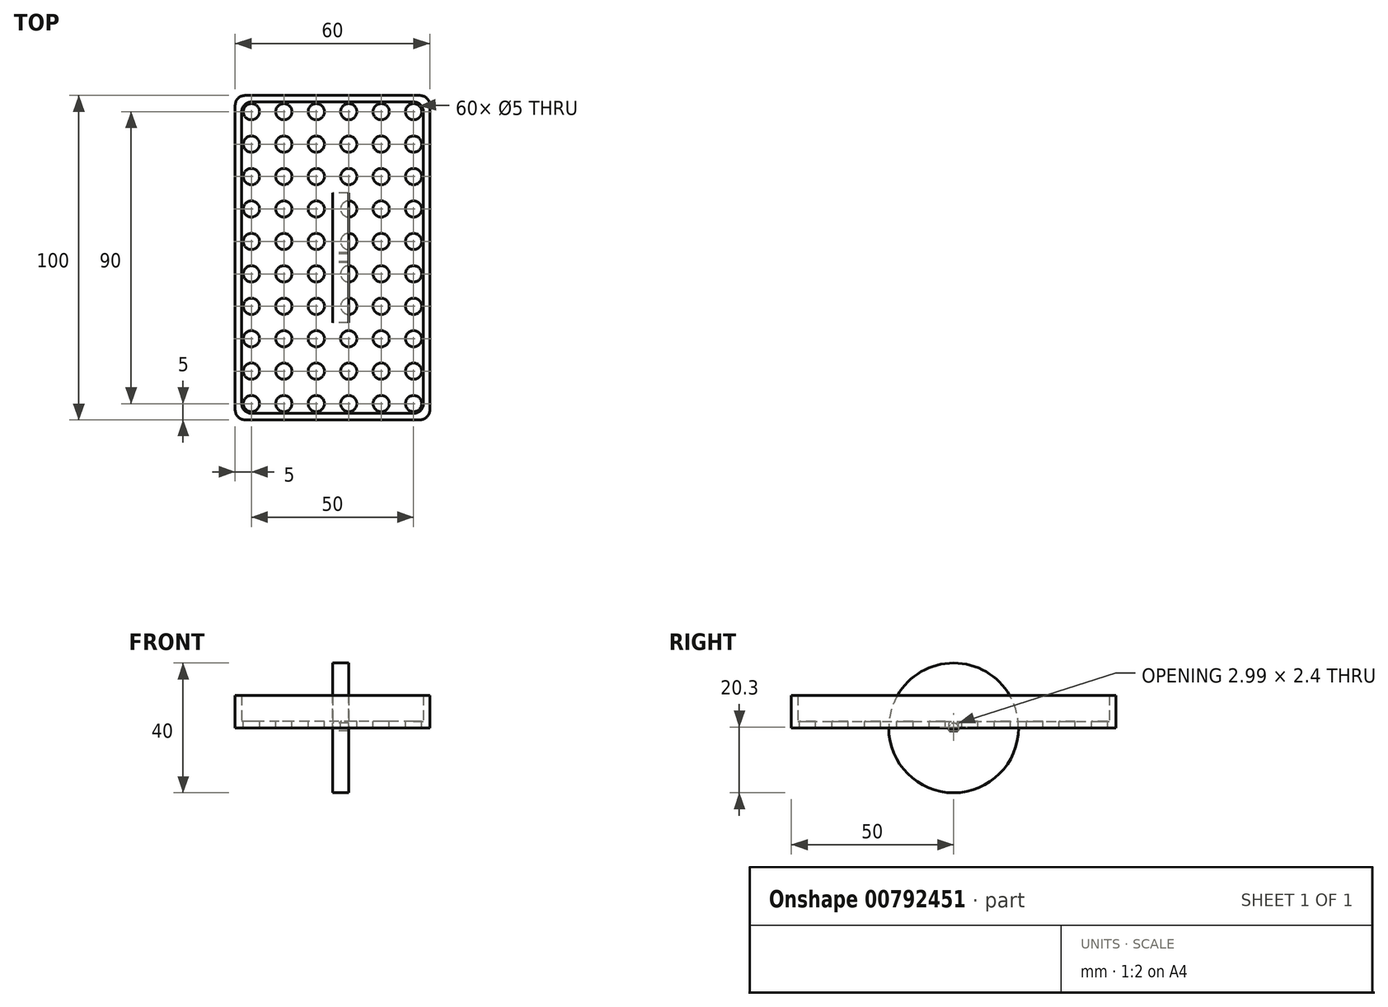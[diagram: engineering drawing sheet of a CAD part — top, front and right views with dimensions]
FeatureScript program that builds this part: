
annotation { "Feature Type Name" : "Feature", "Feature Type Description" : "" }
export const myFeature = defineFeature(function(context is Context, id is Id, definition is map)
    precondition{}
    {
        {
            var Q0;
            Q0=qCreatedBy(makeId("Top.planeOp"),FACE);
            var sketch = newSketch(context, id + "F0", { "sketchPlane" : qUnion([Q0])});
            skLineSegment(sketch, "E0.bottom", {"start": v(30, -50) * mm, "end": v(-30, -50) * mm});
            skLineSegment(sketch, "E0.top", {"start": v(30, 50) * mm, "end": v(-30, 50) * mm});
            skLineSegment(sketch, "E0.left", {"start": v(30, -50) * mm, "end": v(30, 50) * mm});
            skLineSegment(sketch, "E0.right", {"start": v(-30, -50) * mm, "end": v(-30, 50) * mm});
            skPoint(sketch, "E0.middle", {"position": v(0, 0) * mm});
            skSolve(sketch);
        }
        {
            var Q0;
            Q0=makeQuery(id+"F0.imprint","IMPRINT",FACE,{"disambiguationData":[TD([[makeQuery(id+"F0.imprint","IMPRINT",EDGE,{"derivedFrom":sQuery(id+"F0.wireOp",EDGE,"E0.bottom")}),-1.0]])]});
            extrude(context, id + "F1", {"entities" : qUnion([Q0]), "depth" : 10 * mm, "offsetDistance" : 25 * mm});
        }
        {
            var Q0;
            Q0=makeQuery(id+"F1.opExtrude","CAP_FACE",FACE,{"disambiguationData":[OSD([sQuery(id+"F0.wireOp",EDGE,"E0.bottom"),sQuery(id+"F0.wireOp",EDGE,"E0.top"),sQuery(id+"F0.wireOp",EDGE,"E0.left"),sQuery(id+"F0.wireOp",EDGE,"E0.right")])],"isStart":false});
            shell(context, id + "F2", {"entities" : qUnion([Q0]), "thickness" : 2 * mm});
        }
        {
            var Q0;
            Q0=makeQuery(id+"F2.opShell","OFFSET_FACE",FACE,{"disambiguationData":[OSD([sQuery(id+"F0.wireOp",EDGE,"E0.bottom"),sQuery(id+"F0.wireOp",EDGE,"E0.top"),sQuery(id+"F0.wireOp",EDGE,"E0.left"),sQuery(id+"F0.wireOp",EDGE,"E0.right")])]});
            var sketch = newSketch(context, id + "F3", { "sketchPlane" : qUnion([Q0])});
            skPoint(sketch, "E1", {"position": v(-25, 45) * mm});
            skPoint(sketch, "E2.0.1.0", {"position": v(-25, 35) * mm});
            skPoint(sketch, "E2.0.2.0", {"position": v(-25, 25) * mm});
            skPoint(sketch, "E2.0.3.0", {"position": v(-25, 15) * mm});
            skPoint(sketch, "E2.0.4.0", {"position": v(-25, 5) * mm});
            skPoint(sketch, "E2.0.5.0", {"position": v(-25, -5) * mm});
            skPoint(sketch, "E2.0.6.0", {"position": v(-25, -15) * mm});
            skPoint(sketch, "E2.0.7.0", {"position": v(-25, -25) * mm});
            skPoint(sketch, "E2.0.8.0", {"position": v(-25, -35) * mm});
            skPoint(sketch, "E2.0.9.0", {"position": v(-25, -45) * mm});
            skPoint(sketch, "E2.1.0.0", {"position": v(-15, 45) * mm});
            skPoint(sketch, "E2.1.1.0", {"position": v(-15, 35) * mm});
            skPoint(sketch, "E2.1.2.0", {"position": v(-15, 25) * mm});
            skPoint(sketch, "E2.1.3.0", {"position": v(-15, 15) * mm});
            skPoint(sketch, "E2.1.4.0", {"position": v(-15, 5) * mm});
            skPoint(sketch, "E2.1.5.0", {"position": v(-15, -5) * mm});
            skPoint(sketch, "E2.1.6.0", {"position": v(-15, -15) * mm});
            skPoint(sketch, "E2.1.7.0", {"position": v(-15, -25) * mm});
            skPoint(sketch, "E2.1.8.0", {"position": v(-15, -35) * mm});
            skPoint(sketch, "E2.1.9.0", {"position": v(-15, -45) * mm});
            skPoint(sketch, "E2.2.0.0", {"position": v(-5, 45) * mm});
            skPoint(sketch, "E2.2.1.0", {"position": v(-5, 35) * mm});
            skPoint(sketch, "E2.2.2.0", {"position": v(-5, 25) * mm});
            skPoint(sketch, "E2.2.3.0", {"position": v(-5, 15) * mm});
            skPoint(sketch, "E2.2.4.0", {"position": v(-5, 5) * mm});
            skPoint(sketch, "E2.2.5.0", {"position": v(-5, -5) * mm});
            skPoint(sketch, "E2.2.6.0", {"position": v(-5, -15) * mm});
            skPoint(sketch, "E2.2.7.0", {"position": v(-5, -25) * mm});
            skPoint(sketch, "E2.2.8.0", {"position": v(-5, -35) * mm});
            skPoint(sketch, "E2.2.9.0", {"position": v(-5, -45) * mm});
            skPoint(sketch, "E2.3.0.0", {"position": v(5, 45) * mm});
            skPoint(sketch, "E2.3.1.0", {"position": v(5, 35) * mm});
            skPoint(sketch, "E2.3.2.0", {"position": v(5, 25) * mm});
            skPoint(sketch, "E2.3.3.0", {"position": v(5, 15) * mm});
            skPoint(sketch, "E2.3.4.0", {"position": v(5, 5) * mm});
            skPoint(sketch, "E2.3.5.0", {"position": v(5, -5) * mm});
            skPoint(sketch, "E2.3.6.0", {"position": v(5, -15) * mm});
            skPoint(sketch, "E2.3.7.0", {"position": v(5, -25) * mm});
            skPoint(sketch, "E2.3.8.0", {"position": v(5, -35) * mm});
            skPoint(sketch, "E2.3.9.0", {"position": v(5, -45) * mm});
            skPoint(sketch, "E2.4.0.0", {"position": v(15, 45) * mm});
            skPoint(sketch, "E2.4.1.0", {"position": v(15, 35) * mm});
            skPoint(sketch, "E2.4.2.0", {"position": v(15, 25) * mm});
            skPoint(sketch, "E2.4.3.0", {"position": v(15, 15) * mm});
            skPoint(sketch, "E2.4.4.0", {"position": v(15, 5) * mm});
            skPoint(sketch, "E2.4.5.0", {"position": v(15, -5) * mm});
            skPoint(sketch, "E2.4.6.0", {"position": v(15, -15) * mm});
            skPoint(sketch, "E2.4.7.0", {"position": v(15, -25) * mm});
            skPoint(sketch, "E2.4.8.0", {"position": v(15, -35) * mm});
            skPoint(sketch, "E2.4.9.0", {"position": v(15, -45) * mm});
            skPoint(sketch, "E2.5.0.0", {"position": v(25, 45) * mm});
            skPoint(sketch, "E2.5.1.0", {"position": v(25, 35) * mm});
            skPoint(sketch, "E2.5.2.0", {"position": v(25, 25) * mm});
            skPoint(sketch, "E2.5.3.0", {"position": v(25, 15) * mm});
            skPoint(sketch, "E2.5.4.0", {"position": v(25, 5) * mm});
            skPoint(sketch, "E2.5.5.0", {"position": v(25, -5) * mm});
            skPoint(sketch, "E2.5.6.0", {"position": v(25, -15) * mm});
            skPoint(sketch, "E2.5.7.0", {"position": v(25, -25) * mm});
            skPoint(sketch, "E2.5.8.0", {"position": v(25, -35) * mm});
            skPoint(sketch, "E2.5.9.0", {"position": v(25, -45) * mm});
            skLineSegment(sketch, "E2.direction1", {"start": v(-25, 45) * mm, "end": v(-15, 45) * mm, "construction": true});
            skLineSegment(sketch, "E2.direction2", {"start": v(-25, 45) * mm, "end": v(-25, 35) * mm, "construction": true});
            skLineSegment(sketch, "E3", {"start": v(5, 5) * mm, "end": v(-5, -5) * mm, "construction": true});
            skPoint(sketch, "E4", {"position": v(0, 0) * mm});
            skSolve(sketch);
        }
        {
            var Q0;
            Q0=sQuery(id+"F3.wireOp",VERTEX,"E2.1.1.0");
            var Q1;
            Q1=sQuery(id+"F3.wireOp",VERTEX,"E2.4.1.0");
            var Q2;
            Q2=sQuery(id+"F3.wireOp",VERTEX,"E1");
            var Q3;
            Q3=sQuery(id+"F3.wireOp",VERTEX,"E2.1.0.0");
            var Q4;
            Q4=sQuery(id+"F3.wireOp",VERTEX,"E2.2.0.0");
            var Q5;
            Q5=sQuery(id+"F3.wireOp",VERTEX,"E2.3.0.0");
            var Q6;
            Q6=sQuery(id+"F3.wireOp",VERTEX,"E2.4.0.0");
            var Q7;
            Q7=sQuery(id+"F3.wireOp",VERTEX,"E2.5.0.0");
            var Q8;
            Q8=sQuery(id+"F3.wireOp",VERTEX,"E2.3.3.0");
            var Q9;
            Q9=sQuery(id+"F3.wireOp",VERTEX,"E2.1.2.0");
            var Q10;
            Q10=sQuery(id+"F3.wireOp",VERTEX,"E2.5.5.0");
            var Q11;
            Q11=sQuery(id+"F3.wireOp",VERTEX,"E2.1.3.0");
            var Q12;
            Q12=sQuery(id+"F3.wireOp",VERTEX,"E2.3.6.0");
            var Q13;
            Q13=sQuery(id+"F3.wireOp",VERTEX,"E2.1.4.0");
            var Q14;
            Q14=sQuery(id+"F3.wireOp",VERTEX,"E2.5.2.0");
            var Q15;
            Q15=sQuery(id+"F3.wireOp",VERTEX,"E2.4.6.0");
            var Q16;
            Q16=sQuery(id+"F3.wireOp",VERTEX,"E2.0.6.0");
            var Q17;
            Q17=sQuery(id+"F3.wireOp",VERTEX,"E2.4.7.0");
            var Q18;
            Q18=sQuery(id+"F3.wireOp",VERTEX,"E2.0.3.0");
            var Q19;
            Q19=sQuery(id+"F3.wireOp",VERTEX,"E2.3.9.0");
            var Q20;
            Q20=sQuery(id+"F3.wireOp",VERTEX,"E2.4.2.0");
            var Q21;
            Q21=sQuery(id+"F3.wireOp",VERTEX,"E2.0.9.0");
            var Q22;
            Q22=sQuery(id+"F3.wireOp",VERTEX,"E2.1.9.0");
            var Q23;
            Q23=sQuery(id+"F3.wireOp",VERTEX,"E2.4.3.0");
            var Q24;
            Q24=sQuery(id+"F3.wireOp",VERTEX,"E2.2.8.0");
            var Q25;
            Q25=sQuery(id+"F3.wireOp",VERTEX,"E2.5.9.0");
            var Q26;
            Q26=sQuery(id+"F3.wireOp",VERTEX,"E2.direction2.end");
            var Q27;
            Q27=sQuery(id+"F3.wireOp",VERTEX,"E2.2.4.0");
            var Q28;
            Q28=sQuery(id+"F3.wireOp",VERTEX,"E2.2.5.0");
            var Q29;
            Q29=sQuery(id+"F3.wireOp",VERTEX,"E2.4.9.0");
            var Q30;
            Q30=sQuery(id+"F3.wireOp",VERTEX,"E2.5.1.0");
            var Q31;
            Q31=sQuery(id+"F3.wireOp",VERTEX,"E2.3.5.0");
            var Q32;
            Q32=sQuery(id+"F3.wireOp",VERTEX,"E2.0.5.0");
            var Q33;
            Q33=sQuery(id+"F3.wireOp",VERTEX,"E2.4.5.0");
            var Q34;
            Q34=sQuery(id+"F3.wireOp",VERTEX,"E2.0.7.0");
            var Q35;
            Q35=sQuery(id+"F3.wireOp",VERTEX,"E2.1.8.0");
            var Q36;
            Q36=sQuery(id+"F3.wireOp",VERTEX,"E2.2.3.0");
            var Q37;
            Q37=sQuery(id+"F3.wireOp",VERTEX,"E2.5.7.0");
            var Q38;
            Q38=sQuery(id+"F3.wireOp",VERTEX,"E2.2.6.0");
            var Q39;
            Q39=sQuery(id+"F3.wireOp",VERTEX,"E2.3.4.0");
            var Q40;
            Q40=sQuery(id+"F3.wireOp",VERTEX,"E2.3.7.0");
            var Q41;
            Q41=sQuery(id+"F3.wireOp",VERTEX,"E2.5.3.0");
            var Q42;
            Q42=sQuery(id+"F3.wireOp",VERTEX,"E2.3.8.0");
            var Q43;
            Q43=sQuery(id+"F3.wireOp",VERTEX,"E2.5.4.0");
            var Q44;
            Q44=sQuery(id+"F3.wireOp",VERTEX,"E2.2.7.0");
            var Q45;
            Q45=sQuery(id+"F3.wireOp",VERTEX,"E2.0.8.0");
            var Q46;
            Q46=sQuery(id+"F3.wireOp",VERTEX,"E2.1.5.0");
            var Q47;
            Q47=sQuery(id+"F3.wireOp",VERTEX,"E2.1.7.0");
            var Q48;
            Q48=sQuery(id+"F3.wireOp",VERTEX,"E2.3.1.0");
            var Q49;
            Q49=sQuery(id+"F3.wireOp",VERTEX,"E2.2.1.0");
            var Q50;
            Q50=sQuery(id+"F3.wireOp",VERTEX,"E2.0.2.0");
            var Q51;
            Q51=sQuery(id+"F3.wireOp",VERTEX,"E2.2.2.0");
            var Q52;
            Q52=sQuery(id+"F3.wireOp",VERTEX,"E2.5.8.0");
            var Q53;
            Q53=sQuery(id+"F3.wireOp",VERTEX,"E2.1.6.0");
            var Q54;
            Q54=sQuery(id+"F3.wireOp",VERTEX,"E2.3.2.0");
            var Q55;
            Q55=sQuery(id+"F3.wireOp",VERTEX,"E2.4.8.0");
            var Q56;
            Q56=sQuery(id+"F3.wireOp",VERTEX,"E2.5.6.0");
            var Q57;
            Q57=sQuery(id+"F3.wireOp",VERTEX,"E2.0.4.0");
            var Q58;
            Q58=sQuery(id+"F3.wireOp",VERTEX,"E2.4.4.0");
            var Q59;
            Q59=sQuery(id+"F3.wireOp",VERTEX,"E2.2.9.0");
            var Q60;
            Q60=makeQuery(id+"F1.opExtrude","SWEPT_BODY",BODY,{"disambiguationData":[OSD([sQuery(id+"F0.wireOp",EDGE,"E0.bottom"),sQuery(id+"F0.wireOp",EDGE,"E0.top"),sQuery(id+"F0.wireOp",EDGE,"E0.left"),sQuery(id+"F0.wireOp",EDGE,"E0.right")])]});
            hole(context, id + "F4", {"style" : HoleStyle.SIMPLE, "endStyle" : HoleEndStyle.THROUGH, "holeDiameter" : 5 * mm, "majorDiameter" : 5 * mm, "isTappedThrough" : true, "tappedDepth" : 12 * mm, "tapClearance" : 3, "locations" : qUnion([Q0, Q1, Q2, Q3, Q4, Q5, Q6, Q7, Q8, Q9, Q10, Q11, Q12, Q13, Q14, Q15, Q16, Q17, Q18, Q19, Q20, Q21, Q22, Q23, Q24, Q25, Q26, Q27, Q28, Q29, Q30, Q31, Q32, Q33, Q34, Q35, Q36, Q37, Q38, Q39, Q40, Q41, Q42, Q43, Q44, Q45, Q46, Q47, Q48, Q49, Q50, Q51, Q52, Q53, Q54, Q55, Q56, Q57, Q58, Q59]), "scope" : qUnion([Q60])});
        }
        {
            var Q0;
            Q0=makeQuery(id+"F2.opShell","OFFSET_EDGE",EDGE,{"disambiguationData":[OSD([sQuery(id+"F0.wireOp",EDGE,"E0.top"),sQuery(id+"F0.wireOp",EDGE,"E0.right")])]});
            var Q1;
            Q1=makeQuery(id+"F2.opShell","OFFSET_EDGE",EDGE,{"disambiguationData":[OSD([sQuery(id+"F0.wireOp",EDGE,"E0.top"),sQuery(id+"F0.wireOp",EDGE,"E0.left")])]});
            var Q2;
            Q2=makeQuery(id+"F2.opShell","OFFSET_EDGE",EDGE,{"disambiguationData":[OSD([sQuery(id+"F0.wireOp",EDGE,"E0.bottom"),sQuery(id+"F0.wireOp",EDGE,"E0.right")])]});
            var Q3;
            Q3=makeQuery(id+"F2.opShell","OFFSET_EDGE",EDGE,{"disambiguationData":[OSD([sQuery(id+"F0.wireOp",EDGE,"E0.bottom"),sQuery(id+"F0.wireOp",EDGE,"E0.left")])]});
            var Q4;
            Q4=makeQuery(id+"F1.opExtrude","SWEPT_EDGE",EDGE,{"disambiguationData":[OSD([sQuery(id+"F0.wireOp",EDGE,"E0.bottom"),sQuery(id+"F0.wireOp",EDGE,"E0.right")])]});
            var Q5;
            Q5=makeQuery(id+"F1.opExtrude","SWEPT_EDGE",EDGE,{"disambiguationData":[OSD([sQuery(id+"F0.wireOp",EDGE,"E0.bottom"),sQuery(id+"F0.wireOp",EDGE,"E0.left")])]});
            var Q6;
            Q6=makeQuery(id+"F1.opExtrude","SWEPT_EDGE",EDGE,{"disambiguationData":[OSD([sQuery(id+"F0.wireOp",EDGE,"E0.top"),sQuery(id+"F0.wireOp",EDGE,"E0.left")])]});
            var Q7;
            Q7=makeQuery(id+"F1.opExtrude","SWEPT_EDGE",EDGE,{"disambiguationData":[OSD([sQuery(id+"F0.wireOp",EDGE,"E0.top"),sQuery(id+"F0.wireOp",EDGE,"E0.right")])]});
            fillet(context, id + "F5", {"entities" : qUnion([Q0, Q1, Q2, Q3, Q4, Q5, Q6, Q7]), "tangentPropagation" : true, "radius" : 3 * mm, "defaultsChanged" : false, "vertexSettings" : [], "allowEdgeOverflow" : false});
        }
        {
            var Q0;
            Q0=qCreatedBy(makeId("Right.planeOp"),FACE);
            var sketch = newSketch(context, id + "F6", { "sketchPlane" : qUnion([Q0])});
            skCircle(sketch, "E5", {"center": v(0, 0) * mm, "radius": 20 * mm});
            skArc(sketch, "E6", {"start": v(1.2, -0.9) * mm, "mid": v(0, 1.5) * mm, "end": v(-1.2, -0.9) * mm});
            skLineSegment(sketch, "E7", {"start": v(1.2, -0.9) * mm, "end": v(-1.2, -0.9) * mm});
            skPoint(sketch, "E8", {"position": v(0, 1.5) * mm});
            skSolve(sketch);
        }
        {
            var Q0;
            Q0=makeQuery(id+"F6.imprint","IMPRINT",FACE,{"disambiguationData":[TD([[makeQuery(id+"F6.imprint","IMPRINT",EDGE,{"derivedFrom":sQuery(id+"F6.wireOp",EDGE,"E5")}),1.0]])]});
            extrude(context, id + "F7", {"entities" : qUnion([Q0]), "depth" : 5 * mm, "offsetDistance" : 25 * mm});
        }
    });
